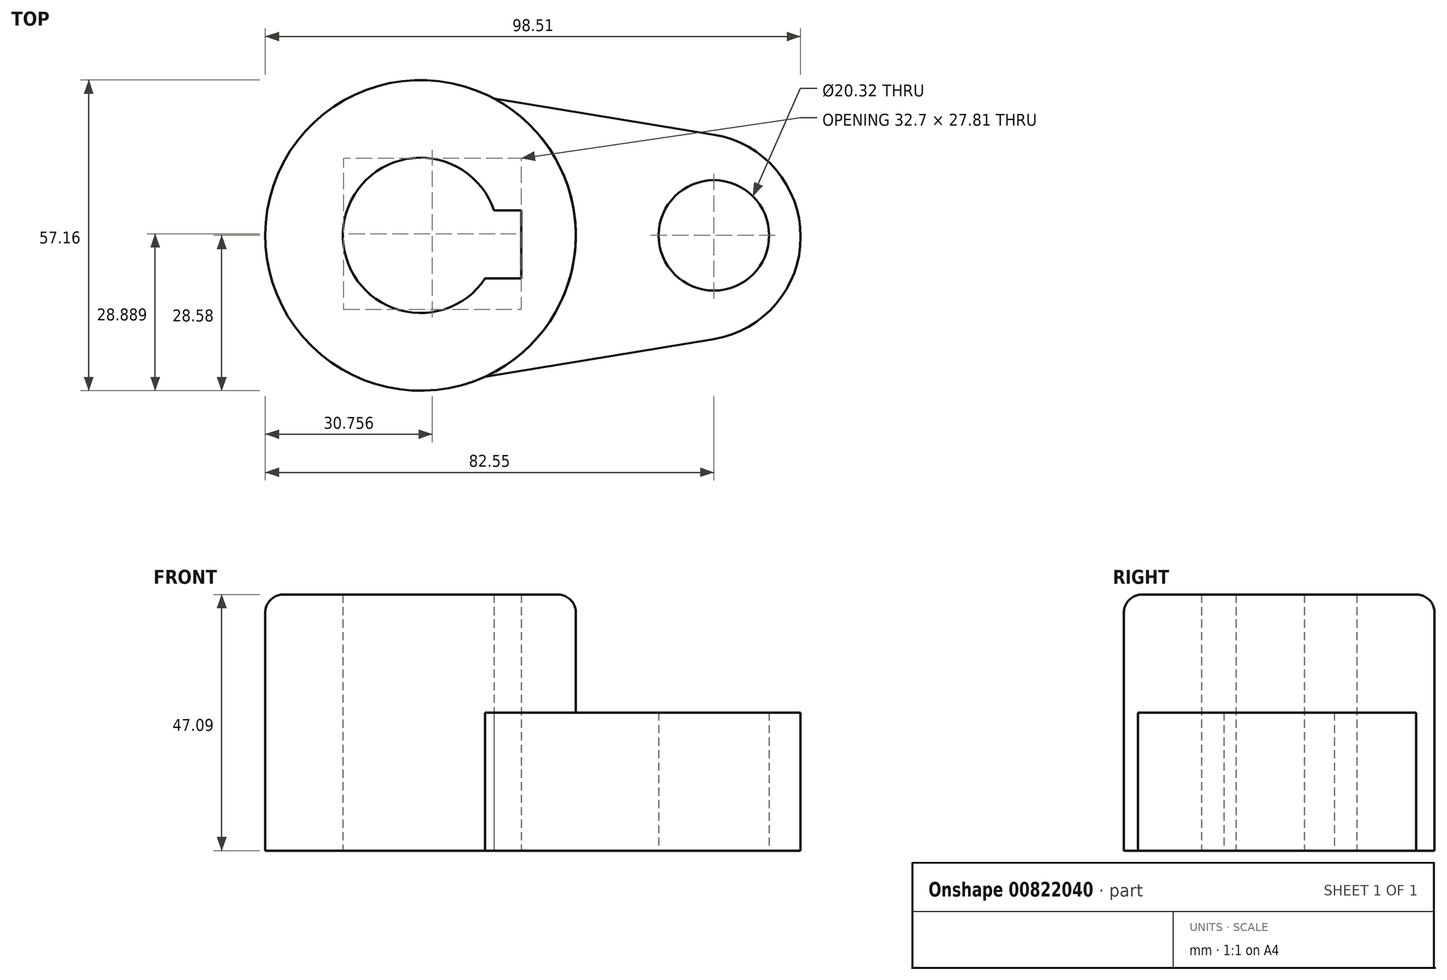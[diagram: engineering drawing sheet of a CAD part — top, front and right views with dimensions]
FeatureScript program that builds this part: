
annotation { "Feature Type Name" : "Feature", "Feature Type Description" : "" }
export const myFeature = defineFeature(function(context is Context, id is Id, definition is map)
    precondition{}
    {
        {
            var Q0;
            Q0=qCreatedBy(makeId("Top.planeOp"),FACE);
            var sketch = newSketch(context, id + "F0", { "sketchPlane" : qUnion([Q0])});
            skCircle(sketch, "E0", {"center": v(-53.98, 0) * mm, "radius": 28.58 * mm});
            skArc(sketch, "E1", {"start": v(-40.45, 4.62) * mm, "mid": v(-68.14, 1.84) * mm, "end": v(-42.09, -7.93) * mm});
            skCircle(sketch, "E2", {"center": v(0, 0) * mm, "radius": 10.16 * mm});
            skLineSegment(sketch, "E3", {"start": v(-40.45, 4.62) * mm, "end": v(-35.45, 4.62) * mm});
            skLineSegment(sketch, "E4", {"start": v(-35.45, 4.62) * mm, "end": v(-35.45, -7.93) * mm});
            skLineSegment(sketch, "E5", {"start": v(-35.45, -7.93) * mm, "end": v(-42.09, -7.93) * mm});
            skLineSegment(sketch, "E6", {"start": v(-42.09, -25.98) * mm, "end": v(0, -19.07) * mm});
            skLineSegment(sketch, "E7", {"start": v(-40.45, 25.17) * mm, "end": v(0, 18.53) * mm});
            skArc(sketch, "E8", {"start": v(0, -19.07) * mm, "mid": v(15.96, -0.27) * mm, "end": v(0, 18.53) * mm});
            skSolve(sketch);
        }
        {
            var Q0;
            Q0=makeQuery(id+"F0.imprint","IMPRINT",FACE,{"disambiguationData":[TD([[makeQuery(id+"F0.imprint","IMPRINT",EDGE,{"derivedFrom":sQuery(id+"F0.wireOp",EDGE,"E1")}),-1.0]])]});
            extrude(context, id + "F1", {"entities" : qUnion([Q0]), "depth" : 47.1 * mm, "offsetDistance" : 25.4 * mm});
        }
        {
            var Q0;
            Q0=makeQuery(id+"F0.imprint","IMPRINT",FACE,{"disambiguationData":[TD([[makeQuery(id+"F0.imprint","IMPRINT",EDGE,{"derivedFrom":sQuery(id+"F0.wireOp",EDGE,"E2")}),-1.0]])]});
            extrude(context, id + "F2", {"entities" : qUnion([Q0]), "operationType" : NewBodyOperationType.ADD, "depth" : 25.4 * mm, "offsetDistance" : 25.4 * mm});
        }
        {
            var Q0;
            Q0=makeQuery(id+"F1.opExtrude","CAP_EDGE",EDGE,{"disambiguationData":[OSD([sQuery(id+"F0.wireOp",EDGE,"E0")])],"isStart":false});
            fillet(context, id + "F3", {"entities" : qUnion([Q0]), "radius" : 3.3 * mm, "tangentPropagation" : true, "allowEdgeOverflow" : false});
        }
    });
